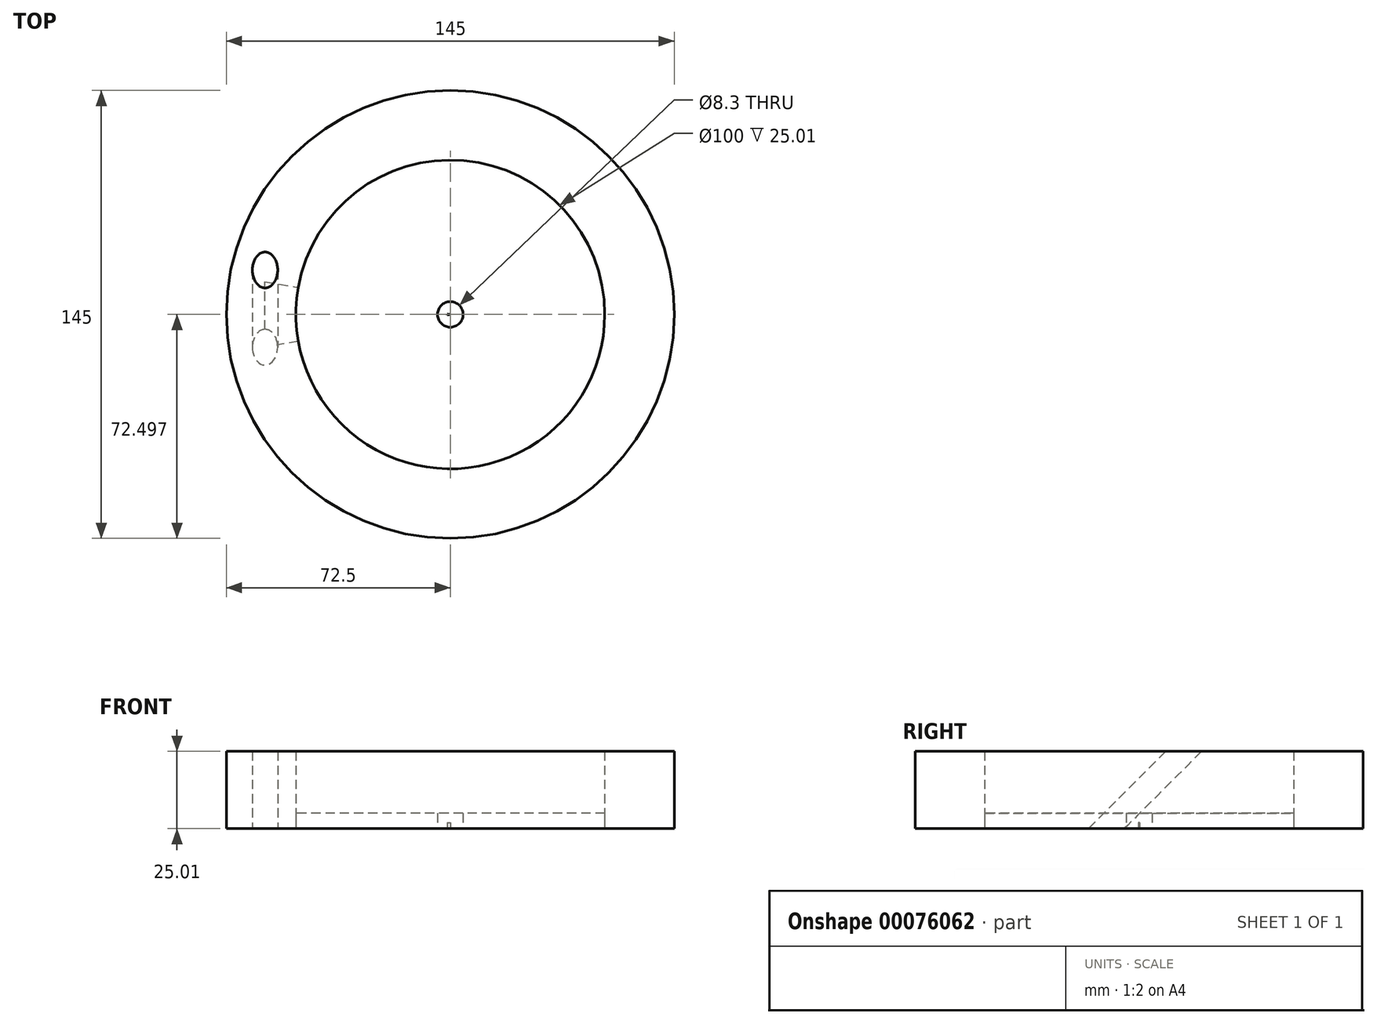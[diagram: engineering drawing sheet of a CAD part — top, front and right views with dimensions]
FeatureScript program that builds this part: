
annotation { "Feature Type Name" : "Feature", "Feature Type Description" : "" }
export const myFeature = defineFeature(function(context is Context, id is Id, definition is map)
    precondition{}
    {
        {
            var Q0;
            Q0=qCreatedBy(makeId("Top.planeOp"),FACE);
            var sketch = newSketch(context, id + "F0", { "sketchPlane" : qUnion([Q0])});
            skCircle(sketch, "E0", {"center": v(0, 0) * mm, "radius": 4.1 * mm});
            skLineSegment(sketch, "E1", {"start": v(0, 0) * mm, "end": v(0, 21.21) * mm});
            skLineSegment(sketch, "E2", {"start": v(0, 21.21) * mm, "end": v(60, 10.6) * mm});
            skLineSegment(sketch, "E3", {"start": v(60, 10.6) * mm, "end": v(0, 0) * mm});
            skCircle(sketch, "E4", {"center": v(60, 10.6) * mm, "radius": 72.5 * mm});
            skCircle(sketch, "E5", {"center": v(60, 10.6) * mm, "radius": 50 * mm});
            skLineSegment(sketch, "E6", {"start": v(59, 10.43) * mm, "end": v(59, 10.78) * mm});
            skCircle(sketch, "E7", {"center": v(60, 10.6) * mm, "radius": 4.15 * mm});
            skLineSegment(sketch, "E8", {"start": v(60, 10.6) * mm, "end": v(7.27, -19.93) * mm});
            skLineSegment(sketch, "E9", {"start": v(0, 0) * mm, "end": v(7.27, -19.93) * mm});
            skSolve(sketch);
        }
        {
            var Q0;
            Q0=qCreatedBy(makeId("Right.planeOp"),FACE);
            var sketch = newSketch(context, id + "F1", { "sketchPlane" : qUnion([Q0])});
            skLineSegment(sketch, "E10", {"start": v(0, 0) * mm, "end": v(35.36, -35.36) * mm});
            skLineSegment(sketch, "E11", {"start": v(0, 0) * mm, "end": v(35.36, 0) * mm});
            skLineSegment(sketch, "E12", {"start": v(35.36, -35.36) * mm, "end": v(35.36, 0) * mm});
            skLineSegment(sketch, "E13", {"start": v(-8.41, 2.61) * mm, "end": v(-2.61, 8.41) * mm});
            skLineSegment(sketch, "E14", {"start": v(0, 0) * mm, "end": v(-7.07, 7.07) * mm});
            skLineSegment(sketch, "E15", {"start": v(7.21, -7.21) * mm, "end": v(1.42, -7.21) * mm});
            skLineSegment(sketch, "E16", {"start": v(7.21, -7.21) * mm, "end": v(7.21, 0) * mm});
            skLineSegment(sketch, "E17", {"start": v(35.36, -35.36) * mm, "end": v(-5.51, 5.51) * mm});
            skLineSegment(sketch, "E18", {"start": v(-8.97, 14.77) * mm, "end": v(-2.61, 8.41) * mm});
            skLineSegment(sketch, "E19", {"start": v(-15.07, 9.27) * mm, "end": v(-8.41, 2.61) * mm});
            skLineSegment(sketch, "E20", {"start": v(-2.61, 8.41) * mm, "end": v(5.8, 0) * mm});
            skLineSegment(sketch, "E21", {"start": v(-8.41, 2.61) * mm, "end": v(1.42, -7.21) * mm});
            skPoint(sketch, "E22.orphan", {"position": v(7.21, 18.24) * mm});
            skPoint(sketch, "E23.orphan", {"position": v(-18.24, -7.21) * mm});
            skLineSegment(sketch, "E24.MirrorCS", {"start": v(-35.36, -35.36) * mm, "end": v(5.51, 5.51) * mm});
            skLineSegment(sketch, "E25.MirrorCS", {"start": v(-35.36, -35.36) * mm, "end": v(-35.36, 0) * mm});
            skLineSegment(sketch, "E26.MirrorCS", {"start": v(0, 0) * mm, "end": v(-35.36, 0) * mm});
            skLineSegment(sketch, "E27.MirrorCS", {"start": v(-7.21, -7.21) * mm, "end": v(-1.42, -7.21) * mm});
            skLineSegment(sketch, "E28.MirrorCS", {"start": v(8.41, 2.61) * mm, "end": v(-1.42, -7.21) * mm});
            skLineSegment(sketch, "E29.MirrorCS", {"start": v(-7.21, -7.21) * mm, "end": v(-7.21, 0) * mm});
            skLineSegment(sketch, "E30.MirrorCS", {"start": v(2.61, 8.41) * mm, "end": v(-5.8, 0) * mm});
            skLineSegment(sketch, "E31.MirrorCS", {"start": v(8.41, 2.61) * mm, "end": v(2.61, 8.41) * mm});
            skLineSegment(sketch, "E32.MirrorCS", {"start": v(15.07, 9.27) * mm, "end": v(8.41, 2.61) * mm});
            skLineSegment(sketch, "E33.MirrorCS", {"start": v(8.97, 14.77) * mm, "end": v(2.61, 8.41) * mm});
            skLineSegment(sketch, "E34.MirrorCS", {"start": v(0, 0) * mm, "end": v(7.07, 7.07) * mm});
            skLineSegment(sketch, "E35.MirrorCS", {"start": v(35.36, 35.36) * mm, "end": v(35.36, 0) * mm});
            skLineSegment(sketch, "E36.MirrorCS", {"start": v(35.36, 35.36) * mm, "end": v(-5.51, -5.51) * mm});
            skLineSegment(sketch, "E37", {"start": v(35.36, 30.48) * mm, "end": v(30.48, 35.36) * mm});
            skLineSegment(sketch, "E38", {"start": v(30.48, 35.36) * mm, "end": v(35.36, 35.36) * mm});
            skSolve(sketch);
        }
        {
            var Q0;
            Q0=makeQuery(id+"F0.imprint","IMPRINT",FACE,{"disambiguationData":[TD([[makeQuery(id+"F0.imprint","IMPRINT",EDGE,{"derivedFrom":sQuery(id+"F0.wireOp",EDGE,"E4")}),1.0]])]});
            var Q1;
            {var subQ1=sQuery(id+"F0.wireOp",EDGE,"E0");var subQ6=sQuery(id+"F0.wireOp",EDGE,"E1");var subQ9=makeQuery(id+"F0.imprint","INTERSECT",VERTEX,{"derivedFrom":[subQ1,subQ6]});Q1=makeQuery(id+"F0.imprint","IMPRINT",FACE,{"disambiguationData":[TD([[makeQuery(id+"F0.imprint","IMPRINT",EDGE,{"disambiguationData":[TD([[subQ9,1.0]])],"derivedFrom":subQ1}),-1.0]])]});}
            var Q2;
            {var subQ0=sQuery(id+"F0.wireOp",EDGE,"E1");var subQ1=sQuery(id+"F0.wireOp",EDGE,"E0");var subQ2=makeQuery(id+"F0.imprint","INTERSECT",VERTEX,{"derivedFrom":[subQ1,subQ0]});Q2=makeQuery(id+"F0.imprint","IMPRINT",FACE,{"disambiguationData":[TD([[makeQuery(id+"F0.imprint","IMPRINT",EDGE,{"disambiguationData":[TD([[subQ2,-1.0]])],"derivedFrom":subQ1}),1.0]])]});}
            var Q3;
            {var subQ0=sQuery(id+"F0.wireOp",EDGE,"E1");var subQ1=sQuery(id+"F0.wireOp",EDGE,"E0");var subQ2=makeQuery(id+"F0.imprint","INTERSECT",VERTEX,{"derivedFrom":[subQ1,subQ0]});Q3=makeQuery(id+"F0.imprint","IMPRINT",FACE,{"disambiguationData":[TD([[makeQuery(id+"F0.imprint","IMPRINT",EDGE,{"disambiguationData":[TD([[subQ2,1.0]])],"derivedFrom":subQ1}),1.0]])]});}
            var Q4;
            {var subQ5=sQuery(id+"F0.wireOp",EDGE,"E3");var subQ6=sQuery(id+"F0.wireOp",EDGE,"E0");var subQ7=makeQuery(id+"F0.imprint","INTERSECT",VERTEX,{"derivedFrom":[subQ6,subQ5]});Q4=makeQuery(id+"F0.imprint","IMPRINT",FACE,{"disambiguationData":[TD([[makeQuery(id+"F0.imprint","IMPRINT",EDGE,{"disambiguationData":[TD([[subQ7,1.0]])],"derivedFrom":subQ6}),-1.0]])]});}
            var Q5;
            {var subQ0=sQuery(id+"F0.wireOp",EDGE,"E3");var subQ1=sQuery(id+"F0.wireOp",EDGE,"E0");var subQ2=makeQuery(id+"F0.imprint","INTERSECT",VERTEX,{"derivedFrom":[subQ1,subQ0]});Q5=makeQuery(id+"F0.imprint","IMPRINT",FACE,{"disambiguationData":[TD([[makeQuery(id+"F0.imprint","IMPRINT",EDGE,{"disambiguationData":[TD([[subQ2,1.0]])],"derivedFrom":subQ1}),1.0]])]});}
            extrude(context, id + "F2", {"entities" : qUnion([Q0, Q1, Q2, Q3, Q4, Q5]), "depth" : 25 * mm});
        }
        {
            var Q0;
            {var subQ1=sQuery(id+"F0.wireOp",EDGE,"E0");var subQ6=sQuery(id+"F0.wireOp",EDGE,"E1");var subQ9=makeQuery(id+"F0.imprint","INTERSECT",VERTEX,{"derivedFrom":[subQ1,subQ6]});Q0=makeQuery(id+"F0.imprint","IMPRINT",FACE,{"disambiguationData":[TD([[makeQuery(id+"F0.imprint","IMPRINT",EDGE,{"disambiguationData":[TD([[subQ9,1.0]])],"derivedFrom":subQ1}),-1.0]])]});}
            var Q1;
            {var subQ0=sQuery(id+"F0.wireOp",EDGE,"E1");var subQ1=sQuery(id+"F0.wireOp",EDGE,"E0");var subQ2=makeQuery(id+"F0.imprint","INTERSECT",VERTEX,{"derivedFrom":[subQ1,subQ0]});Q1=makeQuery(id+"F0.imprint","IMPRINT",FACE,{"disambiguationData":[TD([[makeQuery(id+"F0.imprint","IMPRINT",EDGE,{"disambiguationData":[TD([[subQ2,1.0]])],"derivedFrom":subQ1}),1.0]])]});}
            extrude(context, id + "F3", {"entities" : qUnion([Q0, Q1]), "operationType" : NewBodyOperationType.ADD, "oppositeDirection" : true, "depth" : 0.01 * mm});
        }
        {
            var Q0;
            {var subQ3=sQuery(id+"F0.wireOp",EDGE,"E6");Q0=makeQuery(id+"F0.imprint","IMPRINT",FACE,{"disambiguationData":[TD([[makeQuery(id+"F0.imprint","IMPRINT",EDGE,{"derivedFrom":subQ3}),-1.0]])]});}
            extrude(context, id + "F4", {"entities" : qUnion([Q0]), "depth" : 2 * mm});
        }
        {
            var Q0;
            {var subQ0=sQuery(id+"F0.wireOp",EDGE,"E5");var subQ1=sQuery(id+"F0.wireOp",EDGE,"E2");var subQ2=makeQuery(id+"F0.imprint","INTERSECT",VERTEX,{"derivedFrom":[subQ1,subQ0]});Q0=makeQuery(id+"F0.imprint","IMPRINT",FACE,{"disambiguationData":[TD([[makeQuery(id+"F0.imprint","IMPRINT",EDGE,{"disambiguationData":[TD([[subQ2,-1.0]])],"derivedFrom":subQ1}),1.0]])]});}
            var Q1;
            {var subQ0=sQuery(id+"F0.wireOp",EDGE,"E5");var subQ1=sQuery(id+"F0.wireOp",EDGE,"E2");var subQ2=makeQuery(id+"F0.imprint","INTERSECT",VERTEX,{"derivedFrom":[subQ1,subQ0]});Q1=makeQuery(id+"F0.imprint","IMPRINT",FACE,{"disambiguationData":[TD([[makeQuery(id+"F0.imprint","IMPRINT",EDGE,{"disambiguationData":[TD([[subQ2,-1.0]])],"derivedFrom":subQ1}),-1.0]])]});}
            var Q2;
            {var subQ0=sQuery(id+"F0.wireOp",EDGE,"E7");var subQ1=sQuery(id+"F0.wireOp",EDGE,"E3");var subQ2=makeQuery(id+"F0.imprint","INTERSECT",VERTEX,{"derivedFrom":[subQ1,subQ0]});Q2=makeQuery(id+"F0.imprint","IMPRINT",FACE,{"disambiguationData":[TD([[makeQuery(id+"F0.imprint","IMPRINT",EDGE,{"disambiguationData":[TD([[subQ2,-1.0]])],"derivedFrom":subQ1}),1.0]])]});}
            extrude(context, id + "F5", {"entities" : qUnion([Q0, Q1, Q2]), "depth" : 5 * mm});
        }
        {
            var Q0;
            {var subQ0=sQuery(id+"F1.wireOp",EDGE,"E38");Q0=makeQuery(id+"F1.imprint","IMPRINT",FACE,{"disambiguationData":[TD([[makeQuery(id+"F1.imprint","IMPRINT",EDGE,{"derivedFrom":subQ0}),-1.0]])]});}
            var Q1;
            {var subQ1=sQuery(id+"F1.wireOp",EDGE,"E35.MirrorCS");var subQ3=sQuery(id+"F1.wireOp",EDGE,"E37");var subQ4=makeQuery(id+"F1.imprint","INTERSECT",VERTEX,{"derivedFrom":[subQ1,subQ3]});Q1=makeQuery(id+"F1.imprint","IMPRINT",FACE,{"disambiguationData":[TD([[makeQuery(id+"F1.imprint","IMPRINT",EDGE,{"disambiguationData":[TD([[subQ4,-1.0]])],"derivedFrom":subQ3}),-1.0]])]});}
            extrude(context, id + "F6", {"entities" : qUnion([Q0, Q1]), "depth" : 0.5 * mm});
        }
        {
            var Q0;
            Q0=makeQuery(id+"F6.opExtrude","SWEPT_FACE",FACE,{"disambiguationData":[OSD([sQuery(id+"F1.wireOp",EDGE,"E37")])]});
            var sketch = newSketch(context, id + "F7", { "sketchPlane" : qUnion([Q0])});
            skCircle(sketch, "E39", {"center": v(0, 0) * mm, "radius": 4.1 * mm});
            skSolve(sketch);
        }
        {
            var Q0;
            {var subQ1=sQuery(id+"F1.wireOp",EDGE,"E37");var subQ6=makeQuery(id+"F6.opExtrude","CAP_EDGE",EDGE,{"disambiguationData":[OSD([subQ1])],"isStart":true});Q0=makeQuery(id+"F7.imprint","IMPRINT",FACE,{"disambiguationData":[TD([[makeQuery(id+"F7.imprint","IMPRINT",EDGE,{"derivedFrom":subQ6}),-1.0]])]});}
            var Q1;
            {var subQ1=sQuery(id+"F1.wireOp",EDGE,"E37");var subQ6=makeQuery(id+"F6.opExtrude","CAP_EDGE",EDGE,{"disambiguationData":[OSD([subQ1])],"isStart":true});Q1=makeQuery(id+"F7.imprint","IMPRINT",FACE,{"disambiguationData":[TD([[makeQuery(id+"F7.imprint","IMPRINT",EDGE,{"derivedFrom":subQ6}),1.0]])]});}
            var Q2;
            Q2=sQuery(id+"F1.wireOp",EDGE,"E36.MirrorCS");
            sweep(context, id + "F8", {"operationType" : NewBodyOperationType.REMOVE, "profiles" : qUnion([Q0, Q1]), "path" : qUnion([Q2])});
        }
    });
